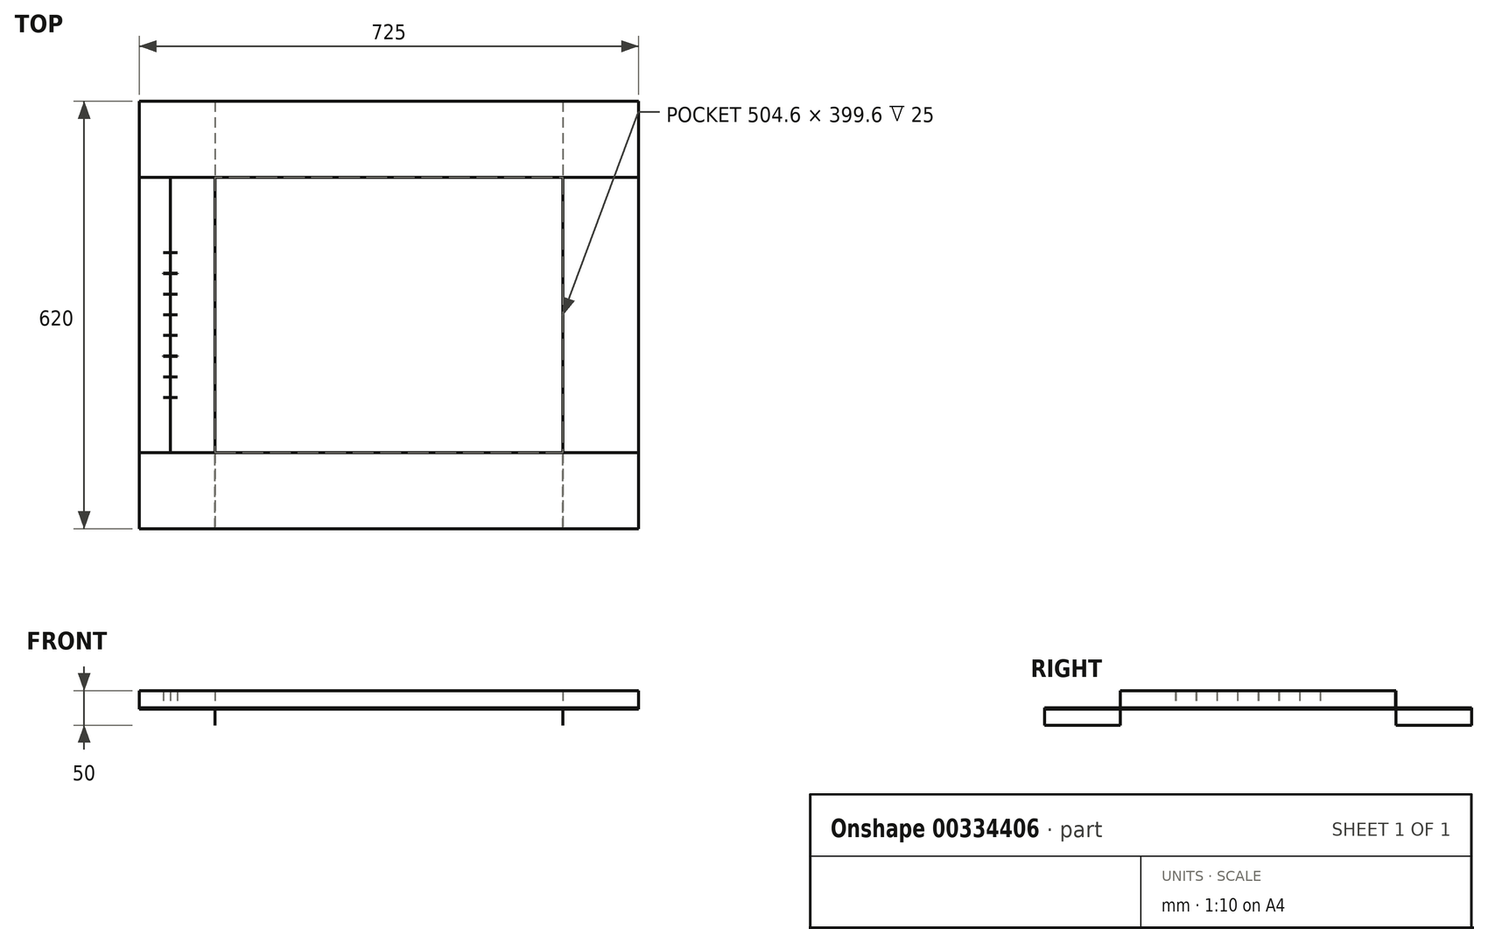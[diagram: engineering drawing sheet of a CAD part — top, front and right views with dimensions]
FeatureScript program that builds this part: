
annotation { "Feature Type Name" : "Feature", "Feature Type Description" : "" }
export const myFeature = defineFeature(function(context is Context, id is Id, definition is map)
    precondition{}
    {
        {
            var Q0;
            Q0=qCreatedBy(makeId("Top.planeOp"),FACE);
            var sketch = newSketch(context, id + "F0", { "sketchPlane" : qUnion([Q0])});
            skLineSegment(sketch, "E0.bottom", {"start": v(0, 0) * mm, "end": v(725, 0) * mm});
            skLineSegment(sketch, "E0.top", {"start": v(0, 620) * mm, "end": v(725, 620) * mm});
            skLineSegment(sketch, "E0.left", {"start": v(0, 0) * mm, "end": v(0, 620) * mm});
            skLineSegment(sketch, "E0.right", {"start": v(725, 0) * mm, "end": v(725, 620) * mm});
            skSolve(sketch);
        }
        {
            var Q0;
            Q0=makeQuery(id+"F0.imprint","IMPRINT",FACE,{"disambiguationData":[TD([[makeQuery(id+"F0.imprint","IMPRINT",EDGE,{"derivedFrom":sQuery(id+"F0.wireOp",EDGE,"E0.bottom")}),1.0]])]});
            extrude(context, id + "F1", {"entities" : qUnion([Q0]), "depth" : 2 * mm});
        }
        {
            var Q0;
            Q0=makeQuery(id+"F1.opExtrude","CAP_FACE",FACE,{"disambiguationData":[OSD([sQuery(id+"F0.wireOp",EDGE,"E0.bottom"),sQuery(id+"F0.wireOp",EDGE,"E0.top"),sQuery(id+"F0.wireOp",EDGE,"E0.left"),sQuery(id+"F0.wireOp",EDGE,"E0.right")])],"isStart":false});
            var sketch = newSketch(context, id + "F2", { "sketchPlane" : qUnion([Q0])});
            skLineSegment(sketch, "E1", {"start": v(0, 510) * mm, "end": v(725, 510) * mm});
            skLineSegment(sketch, "E2", {"start": v(0, 509.8) * mm, "end": v(725, 509.8) * mm});
            skLineSegment(sketch, "E3", {"start": v(0, 110) * mm, "end": v(725, 110) * mm});
            skLineSegment(sketch, "E4", {"start": v(0, 110.2) * mm, "end": v(725, 110.2) * mm});
            skLineSegment(sketch, "E5", {"start": v(615, 620) * mm, "end": v(615, 0) * mm});
            skLineSegment(sketch, "E6", {"start": v(110, 620) * mm, "end": v(110, 0) * mm});
            skLineSegment(sketch, "E7", {"start": v(110.2, 509.8) * mm, "end": v(110.2, 110) * mm});
            skLineSegment(sketch, "E8", {"start": v(614.8, 509.8) * mm, "end": v(614.8, 110) * mm});
            skLineSegment(sketch, "E9", {"start": v(110.25, 620) * mm, "end": v(110.25, 509.8) * mm});
            skLineSegment(sketch, "E10", {"start": v(614.75, 620) * mm, "end": v(614.75, 510) * mm});
            skLineSegment(sketch, "E11", {"start": v(110.25, 0) * mm, "end": v(110.25, 110) * mm});
            skLineSegment(sketch, "E12", {"start": v(614.75, 0) * mm, "end": v(614.75, 110) * mm});
            skLineSegment(sketch, "E13", {"start": v(45.3, 509.8) * mm, "end": v(45.3, 110) * mm});
            skLineSegment(sketch, "E14", {"start": v(45.1, 509.8) * mm, "end": v(45.1, 110) * mm});
            skLineSegment(sketch, "E15", {"start": v(35.3, 460.2) * mm, "end": v(35.3, 460.4) * mm});
            skLineSegment(sketch, "E16", {"start": v(55.3, 460.2) * mm, "end": v(55.3, 460.4) * mm});
            skLineSegment(sketch, "E17.1.0.2", {"start": v(55.3, 430.2) * mm, "end": v(55.3, 430.4) * mm});
            skLineSegment(sketch, "E17.1.0.3", {"start": v(35.3, 430.2) * mm, "end": v(35.3, 430.4) * mm});
            skLineSegment(sketch, "E17.2.0.2", {"start": v(55.3, 400.2) * mm, "end": v(55.3, 400.4) * mm});
            skLineSegment(sketch, "E17.2.0.3", {"start": v(35.3, 400.2) * mm, "end": v(35.3, 400.4) * mm});
            skLineSegment(sketch, "E17.3.0.2", {"start": v(55.3, 370.2) * mm, "end": v(55.3, 370.4) * mm});
            skLineSegment(sketch, "E17.3.0.3", {"start": v(35.3, 370.2) * mm, "end": v(35.3, 370.4) * mm});
            skLineSegment(sketch, "E17.4.0.2", {"start": v(55.3, 340.2) * mm, "end": v(55.3, 340.4) * mm});
            skLineSegment(sketch, "E17.4.0.3", {"start": v(35.3, 340.2) * mm, "end": v(35.3, 340.4) * mm});
            skLineSegment(sketch, "E17.5.0.2", {"start": v(55.3, 310.2) * mm, "end": v(55.3, 310.4) * mm});
            skLineSegment(sketch, "E17.5.0.3", {"start": v(35.3, 310.2) * mm, "end": v(35.3, 310.4) * mm});
            skLineSegment(sketch, "E17.6.0.2", {"start": v(55.3, 280.2) * mm, "end": v(55.3, 280.4) * mm});
            skLineSegment(sketch, "E17.6.0.3", {"start": v(35.3, 280.2) * mm, "end": v(35.3, 280.4) * mm});
            skLineSegment(sketch, "E17.7.0.2", {"start": v(55.3, 250.2) * mm, "end": v(55.3, 250.4) * mm});
            skLineSegment(sketch, "E17.7.0.3", {"start": v(35.3, 250.2) * mm, "end": v(35.3, 250.4) * mm});
            skLineSegment(sketch, "E17.8.0.2", {"start": v(55.3, 220.2) * mm, "end": v(55.3, 220.4) * mm});
            skLineSegment(sketch, "E17.8.0.3", {"start": v(35.3, 220.2) * mm, "end": v(35.3, 220.4) * mm});
            skLineSegment(sketch, "E17.9.0.2", {"start": v(55.3, 190.2) * mm, "end": v(55.3, 190.4) * mm});
            skLineSegment(sketch, "E17.9.0.3", {"start": v(35.3, 190.2) * mm, "end": v(35.3, 190.4) * mm});
            skLineSegment(sketch, "E17.direction1", {"start": v(35.3, 460.4) * mm, "end": v(35.3, 430.4) * mm, "construction": true});
            skLineSegment(sketch, "E18", {"start": v(45.1, 140.64) * mm, "end": v(45.3, 140.64) * mm});
            skLineSegment(sketch, "E19", {"start": v(35.3, 190.4) * mm, "end": v(55.3, 190.4) * mm});
            skLineSegment(sketch, "E20", {"start": v(35.3, 190.2) * mm, "end": v(55.3, 190.2) * mm});
            skLineSegment(sketch, "E21", {"start": v(35.3, 220.4) * mm, "end": v(55.3, 220.4) * mm});
            skLineSegment(sketch, "E22", {"start": v(55.3, 220.2) * mm, "end": v(35.3, 220.2) * mm});
            skLineSegment(sketch, "E23", {"start": v(35.3, 250.4) * mm, "end": v(55.3, 250.4) * mm});
            skLineSegment(sketch, "E24", {"start": v(55.3, 250.2) * mm, "end": v(35.3, 250.2) * mm});
            skLineSegment(sketch, "E25", {"start": v(35.3, 280.4) * mm, "end": v(55.3, 280.4) * mm});
            skLineSegment(sketch, "E26", {"start": v(55.3, 280.2) * mm, "end": v(35.3, 280.2) * mm});
            skLineSegment(sketch, "E27", {"start": v(35.3, 310.4) * mm, "end": v(55.3, 310.4) * mm});
            skLineSegment(sketch, "E28", {"start": v(35.3, 310.2) * mm, "end": v(55.3, 310.2) * mm});
            skLineSegment(sketch, "E29", {"start": v(35.3, 340.4) * mm, "end": v(55.3, 340.4) * mm});
            skLineSegment(sketch, "E30", {"start": v(55.3, 340.2) * mm, "end": v(35.3, 340.2) * mm});
            skLineSegment(sketch, "E31", {"start": v(35.3, 370.4) * mm, "end": v(55.3, 370.4) * mm});
            skLineSegment(sketch, "E32", {"start": v(55.3, 370.2) * mm, "end": v(35.3, 370.2) * mm});
            skLineSegment(sketch, "E33", {"start": v(35.3, 400.4) * mm, "end": v(55.3, 400.4) * mm});
            skLineSegment(sketch, "E34", {"start": v(55.3, 400.2) * mm, "end": v(35.3, 400.2) * mm});
            skSolve(sketch);
        }
        {
            var Q0;
            {var subQ0=sQuery(id+"F2.wireOp",EDGE,"E10");Q0=makeQuery(id+"F2.imprint","IMPRINT",FACE,{"disambiguationData":[TD([[makeQuery(id+"F2.imprint","IMPRINT",EDGE,{"derivedFrom":subQ0}),1.0]])]});}
            var Q1;
            {var subQ0=sQuery(id+"F2.wireOp",EDGE,"E6");var subQ1=sQuery(id+"F2.wireOp",EDGE,"E1");var subQ2=makeQuery(id+"F2.imprint","INTERSECT",VERTEX,{"derivedFrom":[subQ1,subQ0]});Q1=makeQuery(id+"F2.imprint","IMPRINT",FACE,{"disambiguationData":[TD([[makeQuery(id+"F2.imprint","IMPRINT",EDGE,{"disambiguationData":[TD([[subQ2,-1.0]])],"derivedFrom":subQ1}),1.0]])]});}
            var Q2;
            {var subQ0=sQuery(id+"F2.wireOp",EDGE,"E11");Q2=makeQuery(id+"F2.imprint","IMPRINT",FACE,{"disambiguationData":[TD([[makeQuery(id+"F2.imprint","IMPRINT",EDGE,{"derivedFrom":subQ0}),1.0]])]});}
            var Q3;
            {var subQ6=sQuery(id+"F2.wireOp",EDGE,"E12");Q3=makeQuery(id+"F2.imprint","IMPRINT",FACE,{"disambiguationData":[TD([[makeQuery(id+"F2.imprint","IMPRINT",EDGE,{"derivedFrom":subQ6}),-1.0]])]});}
            extrude(context, id + "F3", {"entities" : qUnion([Q0, Q1, Q2, Q3]), "operationType" : NewBodyOperationType.ADD, "oppositeDirection" : true, "depth" : 25 * mm});
        }
        {
            var Q0;
            {var subQ5=makeQuery(id+"F1.opExtrude","CAP_EDGE",EDGE,{"disambiguationData":[OSD([sQuery(id+"F0.wireOp",EDGE,"E0.left")])],"isStart":false});var subQ7=sQuery(id+"F2.wireOp",EDGE,"E1");var subQ8=makeQuery(id+"F2.imprint","INTERSECT",VERTEX,{"derivedFrom":[subQ5,subQ7]});Q0=makeQuery(id+"F2.imprint","IMPRINT",FACE,{"disambiguationData":[TD([[makeQuery(id+"F2.imprint","IMPRINT",EDGE,{"disambiguationData":[TD([[subQ8,-1.0]])],"derivedFrom":subQ7}),-1.0]])]});}
            var Q1;
            {var subQ6=sQuery(id+"F2.wireOp",EDGE,"E1");var subQ8=makeQuery(id+"F2.imprint","INTERSECT",VERTEX,{"derivedFrom":[subQ6,sQuery(id+"F2.wireOp",EDGE,"E10")]});Q1=makeQuery(id+"F2.imprint","IMPRINT",FACE,{"disambiguationData":[TD([[makeQuery(id+"F2.imprint","IMPRINT",EDGE,{"disambiguationData":[TD([[subQ8,1.0]])],"derivedFrom":subQ6}),-1.0]])]});}
            extrude(context, id + "F4", {"entities" : qUnion([Q0, Q1]), "operationType" : NewBodyOperationType.ADD, "depth" : 25 * mm});
        }
        {
            var Q0;
            {var subQ0=sQuery(id+"F2.wireOp",EDGE,"E1");var subQ1=makeQuery(id+"F1.opExtrude","CAP_EDGE",EDGE,{"disambiguationData":[OSD([sQuery(id+"F0.wireOp",EDGE,"E0.right")])],"isStart":false});var subQ2=makeQuery(id+"F2.imprint","INTERSECT",VERTEX,{"derivedFrom":[subQ1,subQ0]});Q0=makeQuery(id+"F2.imprint","IMPRINT",FACE,{"disambiguationData":[TD([[makeQuery(id+"F2.imprint","IMPRINT",EDGE,{"disambiguationData":[TD([[subQ2,1.0]])],"derivedFrom":subQ0}),-1.0]])]});}
            var Q1;
            {var subQ0=sQuery(id+"F2.wireOp",EDGE,"E8");var subQ1=sQuery(id+"F2.wireOp",EDGE,"E2");var subQ2=makeQuery(id+"F2.imprint","INTERSECT",VERTEX,{"derivedFrom":[subQ1,subQ0]});Q1=makeQuery(id+"F2.imprint","IMPRINT",FACE,{"disambiguationData":[TD([[makeQuery(id+"F2.imprint","IMPRINT",EDGE,{"disambiguationData":[TD([[subQ2,-1.0]])],"derivedFrom":subQ1}),-1.0]])]});}
            extrude(context, id + "F5", {"entities" : qUnion([Q0, Q1]), "operationType" : NewBodyOperationType.ADD, "depth" : 25 * mm});
        }
        {
            var Q0;
            {var subQ0=sQuery(id+"F2.wireOp",EDGE,"E3");var subQ1=makeQuery(id+"F1.opExtrude","CAP_EDGE",EDGE,{"disambiguationData":[OSD([sQuery(id+"F0.wireOp",EDGE,"E0.right")])],"isStart":false});var subQ2=makeQuery(id+"F2.imprint","INTERSECT",VERTEX,{"derivedFrom":[subQ1,subQ0]});Q0=makeQuery(id+"F2.imprint","IMPRINT",FACE,{"disambiguationData":[TD([[makeQuery(id+"F2.imprint","IMPRINT",EDGE,{"disambiguationData":[TD([[subQ2,1.0]])],"derivedFrom":subQ0}),1.0]])]});}
            var Q1;
            {var subQ0=sQuery(id+"F2.wireOp",EDGE,"E7");var subQ5=sQuery(id+"F2.wireOp",EDGE,"E3");var subQ9=makeQuery(id+"F2.imprint","INTERSECT",VERTEX,{"derivedFrom":[subQ5,subQ0]});Q1=makeQuery(id+"F2.imprint","IMPRINT",FACE,{"disambiguationData":[TD([[makeQuery(id+"F2.imprint","IMPRINT",EDGE,{"disambiguationData":[TD([[subQ9,-1.0]])],"derivedFrom":subQ5}),1.0]])]});}
            var Q2;
            {var subQ0=sQuery(id+"F2.wireOp",EDGE,"E8");var subQ1=sQuery(id+"F2.wireOp",EDGE,"E3");var subQ2=makeQuery(id+"F2.imprint","INTERSECT",VERTEX,{"derivedFrom":[subQ1,subQ0]});Q2=makeQuery(id+"F2.imprint","IMPRINT",FACE,{"disambiguationData":[TD([[makeQuery(id+"F2.imprint","IMPRINT",EDGE,{"disambiguationData":[TD([[subQ2,-1.0]])],"derivedFrom":subQ1}),1.0]])]});}
            var Q3;
            {var subQ0=sQuery(id+"F2.wireOp",EDGE,"E13");var subQ1=sQuery(id+"F2.wireOp",EDGE,"E3");var subQ2=makeQuery(id+"F2.imprint","INTERSECT",VERTEX,{"derivedFrom":[subQ1,subQ0]});Q3=makeQuery(id+"F2.imprint","IMPRINT",FACE,{"disambiguationData":[TD([[makeQuery(id+"F2.imprint","IMPRINT",EDGE,{"disambiguationData":[TD([[subQ2,-1.0]])],"derivedFrom":subQ1}),1.0]])]});}
            var Q4;
            {var subQ0=sQuery(id+"F2.wireOp",EDGE,"E7");var subQ1=sQuery(id+"F2.wireOp",EDGE,"E3");var subQ2=makeQuery(id+"F2.imprint","INTERSECT",VERTEX,{"derivedFrom":[subQ1,subQ0]});Q4=makeQuery(id+"F2.imprint","IMPRINT",FACE,{"disambiguationData":[TD([[makeQuery(id+"F2.imprint","IMPRINT",EDGE,{"disambiguationData":[TD([[subQ2,1.0]])],"derivedFrom":subQ1}),1.0]])]});}
            extrude(context, id + "F6", {"entities" : qUnion([Q0, Q1, Q2, Q3, Q4]), "operationType" : NewBodyOperationType.ADD, "depth" : 25 * mm});
        }
        {
            var Q0;
            {var subQ0=sQuery(id+"F2.wireOp",EDGE,"E3");var subQ1=makeQuery(id+"F1.opExtrude","CAP_EDGE",EDGE,{"disambiguationData":[OSD([sQuery(id+"F0.wireOp",EDGE,"E0.left")])],"isStart":false});var subQ2=makeQuery(id+"F2.imprint","INTERSECT",VERTEX,{"derivedFrom":[subQ1,subQ0]});Q0=makeQuery(id+"F2.imprint","IMPRINT",FACE,{"disambiguationData":[TD([[makeQuery(id+"F2.imprint","IMPRINT",EDGE,{"disambiguationData":[TD([[subQ2,-1.0]])],"derivedFrom":subQ0}),1.0]])]});}
            extrude(context, id + "F7", {"entities" : qUnion([Q0]), "operationType" : NewBodyOperationType.ADD, "depth" : 25 * mm});
        }
        {
            var Q0;
            {var subQ0=sQuery(id+"F2.wireOp",EDGE,"E18");Q0=makeQuery(id+"F2.imprint","IMPRINT",FACE,{"disambiguationData":[TD([[makeQuery(id+"F2.imprint","IMPRINT",EDGE,{"derivedFrom":subQ0}),1.0]])]});}
            extrude(context, id + "F8", {"entities" : qUnion([Q0]), "operationType" : NewBodyOperationType.ADD, "depth" : 25 * mm});
        }
        {
            var Q0;
            {var subQ0=sQuery(id+"F2.wireOp",EDGE,"E18");Q0=makeQuery(id+"F2.imprint","IMPRINT",FACE,{"disambiguationData":[TD([[makeQuery(id+"F2.imprint","IMPRINT",EDGE,{"derivedFrom":subQ0}),1.0]])]});}
            var Q1;
            {var subQ5=sQuery(id+"F2.wireOp",EDGE,"E17.9.0.3");Q1=makeQuery(id+"F2.imprint","IMPRINT",FACE,{"disambiguationData":[TD([[makeQuery(id+"F2.imprint","IMPRINT",EDGE,{"derivedFrom":subQ5}),-1.0]])]});}
            var Q2;
            {var subQ5=sQuery(id+"F2.wireOp",EDGE,"E17.9.0.2");Q2=makeQuery(id+"F2.imprint","IMPRINT",FACE,{"disambiguationData":[TD([[makeQuery(id+"F2.imprint","IMPRINT",EDGE,{"derivedFrom":subQ5}),1.0]])]});}
            var Q3;
            {var subQ0=sQuery(id+"F2.wireOp",EDGE,"E17.8.0.0");var subQ1=sQuery(id+"F2.wireOp",EDGE,"E13");var subQ2=makeQuery(id+"F2.imprint","INTERSECT",VERTEX,{"derivedFrom":[subQ1,subQ0]});Q3=makeQuery(id+"F2.imprint","IMPRINT",FACE,{"disambiguationData":[TD([[makeQuery(id+"F2.imprint","IMPRINT",EDGE,{"disambiguationData":[TD([[subQ2,-1.0]])],"derivedFrom":subQ1}),-1.0]])]});}
            var Q4;
            {var subQ0=sQuery(id+"F2.wireOp",EDGE,"E17.9.0.1");var subQ1=sQuery(id+"F2.wireOp",EDGE,"E13");var subQ2=makeQuery(id+"F2.imprint","INTERSECT",VERTEX,{"derivedFrom":[subQ1,subQ0]});Q4=makeQuery(id+"F2.imprint","IMPRINT",FACE,{"disambiguationData":[TD([[makeQuery(id+"F2.imprint","IMPRINT",EDGE,{"disambiguationData":[TD([[subQ2,-1.0]])],"derivedFrom":subQ1}),-1.0]])]});}
            var Q5;
            {var subQ5=sQuery(id+"F2.wireOp",EDGE,"E17.8.0.3");Q5=makeQuery(id+"F2.imprint","IMPRINT",FACE,{"disambiguationData":[TD([[makeQuery(id+"F2.imprint","IMPRINT",EDGE,{"derivedFrom":subQ5}),-1.0]])]});}
            var Q6;
            {var subQ5=sQuery(id+"F2.wireOp",EDGE,"E17.8.0.2");Q6=makeQuery(id+"F2.imprint","IMPRINT",FACE,{"disambiguationData":[TD([[makeQuery(id+"F2.imprint","IMPRINT",EDGE,{"derivedFrom":subQ5}),1.0]])]});}
            var Q7;
            {var subQ0=sQuery(id+"F2.wireOp",EDGE,"E17.8.0.1");var subQ1=sQuery(id+"F2.wireOp",EDGE,"E13");var subQ2=makeQuery(id+"F2.imprint","INTERSECT",VERTEX,{"derivedFrom":[subQ1,subQ0]});Q7=makeQuery(id+"F2.imprint","IMPRINT",FACE,{"disambiguationData":[TD([[makeQuery(id+"F2.imprint","IMPRINT",EDGE,{"disambiguationData":[TD([[subQ2,-1.0]])],"derivedFrom":subQ1}),-1.0]])]});}
            var Q8;
            {var subQ0=sQuery(id+"F2.wireOp",EDGE,"E17.7.0.0");var subQ1=sQuery(id+"F2.wireOp",EDGE,"E13");var subQ2=makeQuery(id+"F2.imprint","INTERSECT",VERTEX,{"derivedFrom":[subQ1,subQ0]});Q8=makeQuery(id+"F2.imprint","IMPRINT",FACE,{"disambiguationData":[TD([[makeQuery(id+"F2.imprint","IMPRINT",EDGE,{"disambiguationData":[TD([[subQ2,-1.0]])],"derivedFrom":subQ1}),-1.0]])]});}
            var Q9;
            {var subQ5=sQuery(id+"F2.wireOp",EDGE,"E17.7.0.3");Q9=makeQuery(id+"F2.imprint","IMPRINT",FACE,{"disambiguationData":[TD([[makeQuery(id+"F2.imprint","IMPRINT",EDGE,{"derivedFrom":subQ5}),-1.0]])]});}
            var Q10;
            {var subQ5=sQuery(id+"F2.wireOp",EDGE,"E17.7.0.2");Q10=makeQuery(id+"F2.imprint","IMPRINT",FACE,{"disambiguationData":[TD([[makeQuery(id+"F2.imprint","IMPRINT",EDGE,{"derivedFrom":subQ5}),1.0]])]});}
            var Q11;
            {var subQ0=sQuery(id+"F2.wireOp",EDGE,"E17.7.0.1");var subQ1=sQuery(id+"F2.wireOp",EDGE,"E13");var subQ2=makeQuery(id+"F2.imprint","INTERSECT",VERTEX,{"derivedFrom":[subQ1,subQ0]});Q11=makeQuery(id+"F2.imprint","IMPRINT",FACE,{"disambiguationData":[TD([[makeQuery(id+"F2.imprint","IMPRINT",EDGE,{"disambiguationData":[TD([[subQ2,-1.0]])],"derivedFrom":subQ1}),-1.0]])]});}
            var Q12;
            {var subQ0=sQuery(id+"F2.wireOp",EDGE,"E17.6.0.0");var subQ1=sQuery(id+"F2.wireOp",EDGE,"E13");var subQ2=makeQuery(id+"F2.imprint","INTERSECT",VERTEX,{"derivedFrom":[subQ1,subQ0]});Q12=makeQuery(id+"F2.imprint","IMPRINT",FACE,{"disambiguationData":[TD([[makeQuery(id+"F2.imprint","IMPRINT",EDGE,{"disambiguationData":[TD([[subQ2,-1.0]])],"derivedFrom":subQ1}),-1.0]])]});}
            var Q13;
            {var subQ5=sQuery(id+"F2.wireOp",EDGE,"E17.6.0.3");Q13=makeQuery(id+"F2.imprint","IMPRINT",FACE,{"disambiguationData":[TD([[makeQuery(id+"F2.imprint","IMPRINT",EDGE,{"derivedFrom":subQ5}),-1.0]])]});}
            var Q14;
            {var subQ5=sQuery(id+"F2.wireOp",EDGE,"E17.6.0.2");Q14=makeQuery(id+"F2.imprint","IMPRINT",FACE,{"disambiguationData":[TD([[makeQuery(id+"F2.imprint","IMPRINT",EDGE,{"derivedFrom":subQ5}),1.0]])]});}
            var Q15;
            {var subQ0=sQuery(id+"F2.wireOp",EDGE,"E17.6.0.1");var subQ1=sQuery(id+"F2.wireOp",EDGE,"E13");var subQ2=makeQuery(id+"F2.imprint","INTERSECT",VERTEX,{"derivedFrom":[subQ1,subQ0]});Q15=makeQuery(id+"F2.imprint","IMPRINT",FACE,{"disambiguationData":[TD([[makeQuery(id+"F2.imprint","IMPRINT",EDGE,{"disambiguationData":[TD([[subQ2,-1.0]])],"derivedFrom":subQ1}),-1.0]])]});}
            var Q16;
            {var subQ0=sQuery(id+"F2.wireOp",EDGE,"E17.5.0.0");var subQ1=sQuery(id+"F2.wireOp",EDGE,"E13");var subQ2=makeQuery(id+"F2.imprint","INTERSECT",VERTEX,{"derivedFrom":[subQ1,subQ0]});Q16=makeQuery(id+"F2.imprint","IMPRINT",FACE,{"disambiguationData":[TD([[makeQuery(id+"F2.imprint","IMPRINT",EDGE,{"disambiguationData":[TD([[subQ2,-1.0]])],"derivedFrom":subQ1}),-1.0]])]});}
            var Q17;
            {var subQ5=sQuery(id+"F2.wireOp",EDGE,"E17.5.0.3");Q17=makeQuery(id+"F2.imprint","IMPRINT",FACE,{"disambiguationData":[TD([[makeQuery(id+"F2.imprint","IMPRINT",EDGE,{"derivedFrom":subQ5}),-1.0]])]});}
            var Q18;
            {var subQ0=sQuery(id+"F2.wireOp",EDGE,"E17.5.0.1");var subQ1=sQuery(id+"F2.wireOp",EDGE,"E13");var subQ2=makeQuery(id+"F2.imprint","INTERSECT",VERTEX,{"derivedFrom":[subQ1,subQ0]});Q18=makeQuery(id+"F2.imprint","IMPRINT",FACE,{"disambiguationData":[TD([[makeQuery(id+"F2.imprint","IMPRINT",EDGE,{"disambiguationData":[TD([[subQ2,-1.0]])],"derivedFrom":subQ1}),-1.0]])]});}
            var Q19;
            {var subQ5=sQuery(id+"F2.wireOp",EDGE,"E17.5.0.2");Q19=makeQuery(id+"F2.imprint","IMPRINT",FACE,{"disambiguationData":[TD([[makeQuery(id+"F2.imprint","IMPRINT",EDGE,{"derivedFrom":subQ5}),1.0]])]});}
            var Q20;
            {var subQ0=sQuery(id+"F2.wireOp",EDGE,"E17.4.0.0");var subQ1=sQuery(id+"F2.wireOp",EDGE,"E13");var subQ2=makeQuery(id+"F2.imprint","INTERSECT",VERTEX,{"derivedFrom":[subQ1,subQ0]});Q20=makeQuery(id+"F2.imprint","IMPRINT",FACE,{"disambiguationData":[TD([[makeQuery(id+"F2.imprint","IMPRINT",EDGE,{"disambiguationData":[TD([[subQ2,-1.0]])],"derivedFrom":subQ1}),-1.0]])]});}
            var Q21;
            {var subQ5=sQuery(id+"F2.wireOp",EDGE,"E17.4.0.3");Q21=makeQuery(id+"F2.imprint","IMPRINT",FACE,{"disambiguationData":[TD([[makeQuery(id+"F2.imprint","IMPRINT",EDGE,{"derivedFrom":subQ5}),-1.0]])]});}
            var Q22;
            {var subQ0=sQuery(id+"F2.wireOp",EDGE,"E17.4.0.1");var subQ1=sQuery(id+"F2.wireOp",EDGE,"E13");var subQ2=makeQuery(id+"F2.imprint","INTERSECT",VERTEX,{"derivedFrom":[subQ1,subQ0]});Q22=makeQuery(id+"F2.imprint","IMPRINT",FACE,{"disambiguationData":[TD([[makeQuery(id+"F2.imprint","IMPRINT",EDGE,{"disambiguationData":[TD([[subQ2,-1.0]])],"derivedFrom":subQ1}),-1.0]])]});}
            var Q23;
            {var subQ5=sQuery(id+"F2.wireOp",EDGE,"E17.4.0.2");Q23=makeQuery(id+"F2.imprint","IMPRINT",FACE,{"disambiguationData":[TD([[makeQuery(id+"F2.imprint","IMPRINT",EDGE,{"derivedFrom":subQ5}),1.0]])]});}
            var Q24;
            {var subQ0=sQuery(id+"F2.wireOp",EDGE,"E17.3.0.0");var subQ1=sQuery(id+"F2.wireOp",EDGE,"E13");var subQ2=makeQuery(id+"F2.imprint","INTERSECT",VERTEX,{"derivedFrom":[subQ1,subQ0]});Q24=makeQuery(id+"F2.imprint","IMPRINT",FACE,{"disambiguationData":[TD([[makeQuery(id+"F2.imprint","IMPRINT",EDGE,{"disambiguationData":[TD([[subQ2,-1.0]])],"derivedFrom":subQ1}),-1.0]])]});}
            var Q25;
            {var subQ5=sQuery(id+"F2.wireOp",EDGE,"E17.3.0.3");Q25=makeQuery(id+"F2.imprint","IMPRINT",FACE,{"disambiguationData":[TD([[makeQuery(id+"F2.imprint","IMPRINT",EDGE,{"derivedFrom":subQ5}),-1.0]])]});}
            var Q26;
            {var subQ0=sQuery(id+"F2.wireOp",EDGE,"E17.3.0.1");var subQ1=sQuery(id+"F2.wireOp",EDGE,"E13");var subQ2=makeQuery(id+"F2.imprint","INTERSECT",VERTEX,{"derivedFrom":[subQ1,subQ0]});Q26=makeQuery(id+"F2.imprint","IMPRINT",FACE,{"disambiguationData":[TD([[makeQuery(id+"F2.imprint","IMPRINT",EDGE,{"disambiguationData":[TD([[subQ2,-1.0]])],"derivedFrom":subQ1}),-1.0]])]});}
            var Q27;
            {var subQ5=sQuery(id+"F2.wireOp",EDGE,"E17.3.0.2");Q27=makeQuery(id+"F2.imprint","IMPRINT",FACE,{"disambiguationData":[TD([[makeQuery(id+"F2.imprint","IMPRINT",EDGE,{"derivedFrom":subQ5}),1.0]])]});}
            var Q28;
            {var subQ0=sQuery(id+"F2.wireOp",EDGE,"E17.2.0.0");var subQ1=sQuery(id+"F2.wireOp",EDGE,"E13");var subQ2=makeQuery(id+"F2.imprint","INTERSECT",VERTEX,{"derivedFrom":[subQ1,subQ0]});Q28=makeQuery(id+"F2.imprint","IMPRINT",FACE,{"disambiguationData":[TD([[makeQuery(id+"F2.imprint","IMPRINT",EDGE,{"disambiguationData":[TD([[subQ2,-1.0]])],"derivedFrom":subQ1}),-1.0]])]});}
            var Q29;
            {var subQ5=sQuery(id+"F2.wireOp",EDGE,"E17.2.0.3");Q29=makeQuery(id+"F2.imprint","IMPRINT",FACE,{"disambiguationData":[TD([[makeQuery(id+"F2.imprint","IMPRINT",EDGE,{"derivedFrom":subQ5}),-1.0]])]});}
            var Q30;
            {var subQ0=sQuery(id+"F2.wireOp",EDGE,"E17.2.0.1");var subQ1=sQuery(id+"F2.wireOp",EDGE,"E13");var subQ2=makeQuery(id+"F2.imprint","INTERSECT",VERTEX,{"derivedFrom":[subQ1,subQ0]});Q30=makeQuery(id+"F2.imprint","IMPRINT",FACE,{"disambiguationData":[TD([[makeQuery(id+"F2.imprint","IMPRINT",EDGE,{"disambiguationData":[TD([[subQ2,-1.0]])],"derivedFrom":subQ1}),-1.0]])]});}
            var Q31;
            {var subQ5=sQuery(id+"F2.wireOp",EDGE,"E17.2.0.2");Q31=makeQuery(id+"F2.imprint","IMPRINT",FACE,{"disambiguationData":[TD([[makeQuery(id+"F2.imprint","IMPRINT",EDGE,{"derivedFrom":subQ5}),1.0]])]});}
            var Q32;
            {var subQ0=sQuery(id+"F2.wireOp",EDGE,"E17.1.0.0");var subQ1=sQuery(id+"F2.wireOp",EDGE,"E13");var subQ2=makeQuery(id+"F2.imprint","INTERSECT",VERTEX,{"derivedFrom":[subQ1,subQ0]});Q32=makeQuery(id+"F2.imprint","IMPRINT",FACE,{"disambiguationData":[TD([[makeQuery(id+"F2.imprint","IMPRINT",EDGE,{"disambiguationData":[TD([[subQ2,-1.0]])],"derivedFrom":subQ1}),-1.0]])]});}
            var Q33;
            {var subQ5=sQuery(id+"F2.wireOp",EDGE,"E17.1.0.3");Q33=makeQuery(id+"F2.imprint","IMPRINT",FACE,{"disambiguationData":[TD([[makeQuery(id+"F2.imprint","IMPRINT",EDGE,{"derivedFrom":subQ5}),-1.0]])]});}
            var Q34;
            {var subQ0=sQuery(id+"F2.wireOp",EDGE,"E17.1.0.1");var subQ1=sQuery(id+"F2.wireOp",EDGE,"E13");var subQ2=makeQuery(id+"F2.imprint","INTERSECT",VERTEX,{"derivedFrom":[subQ1,subQ0]});Q34=makeQuery(id+"F2.imprint","IMPRINT",FACE,{"disambiguationData":[TD([[makeQuery(id+"F2.imprint","IMPRINT",EDGE,{"disambiguationData":[TD([[subQ2,-1.0]])],"derivedFrom":subQ1}),-1.0]])]});}
            var Q35;
            {var subQ5=sQuery(id+"F2.wireOp",EDGE,"E17.1.0.2");Q35=makeQuery(id+"F2.imprint","IMPRINT",FACE,{"disambiguationData":[TD([[makeQuery(id+"F2.imprint","IMPRINT",EDGE,{"derivedFrom":subQ5}),1.0]])]});}
            var Q36;
            {var subQ0=sQuery(id+"F2.wireOp",EDGE,"PF9Whc2X-JOV0-p4xt-AjMA-3nAZ7eqoeYj6");var subQ1=sQuery(id+"F2.wireOp",EDGE,"E13");var subQ2=makeQuery(id+"F2.imprint","INTERSECT",VERTEX,{"derivedFrom":[subQ1,subQ0]});Q36=makeQuery(id+"F2.imprint","IMPRINT",FACE,{"disambiguationData":[TD([[makeQuery(id+"F2.imprint","IMPRINT",EDGE,{"disambiguationData":[TD([[subQ2,-1.0]])],"derivedFrom":subQ1}),-1.0]])]});}
            var Q37;
            {var subQ5=sQuery(id+"F2.wireOp",EDGE,"E15");Q37=makeQuery(id+"F2.imprint","IMPRINT",FACE,{"disambiguationData":[TD([[makeQuery(id+"F2.imprint","IMPRINT",EDGE,{"derivedFrom":subQ5}),-1.0]])]});}
            var Q38;
            {var subQ0=sQuery(id+"F2.wireOp",EDGE,"TrYL828V-23KU-50iI-e81v-BixSrFEmtcK7");var subQ1=sQuery(id+"F2.wireOp",EDGE,"E13");var subQ2=makeQuery(id+"F2.imprint","INTERSECT",VERTEX,{"derivedFrom":[subQ1,subQ0]});Q38=makeQuery(id+"F2.imprint","IMPRINT",FACE,{"disambiguationData":[TD([[makeQuery(id+"F2.imprint","IMPRINT",EDGE,{"disambiguationData":[TD([[subQ2,-1.0]])],"derivedFrom":subQ1}),-1.0]])]});}
            var Q39;
            {var subQ5=sQuery(id+"F2.wireOp",EDGE,"E16");Q39=makeQuery(id+"F2.imprint","IMPRINT",FACE,{"disambiguationData":[TD([[makeQuery(id+"F2.imprint","IMPRINT",EDGE,{"derivedFrom":subQ5}),1.0]])]});}
            var Q40;
            {var subQ0=sQuery(id+"F2.wireOp",EDGE,"E13");var subQ1=sQuery(id+"F2.wireOp",EDGE,"E2");var subQ2=makeQuery(id+"F2.imprint","INTERSECT",VERTEX,{"derivedFrom":[subQ1,subQ0]});Q40=makeQuery(id+"F2.imprint","IMPRINT",FACE,{"disambiguationData":[TD([[makeQuery(id+"F2.imprint","IMPRINT",EDGE,{"disambiguationData":[TD([[subQ2,1.0]])],"derivedFrom":subQ1}),-1.0]])]});}
            var Q41;
            {var subQ0=sQuery(id+"F2.wireOp",EDGE,"E7");var subQ1=sQuery(id+"F2.wireOp",EDGE,"E2");var subQ2=makeQuery(id+"F2.imprint","INTERSECT",VERTEX,{"derivedFrom":[subQ1,subQ0]});Q41=makeQuery(id+"F2.imprint","IMPRINT",FACE,{"disambiguationData":[TD([[makeQuery(id+"F2.imprint","IMPRINT",EDGE,{"disambiguationData":[TD([[subQ2,1.0]])],"derivedFrom":subQ1}),-1.0]])]});}
            var Q42;
            {var subQ0=sQuery(id+"F2.wireOp",EDGE,"E6");var subQ1=sQuery(id+"F2.wireOp",EDGE,"E1");var subQ2=makeQuery(id+"F2.imprint","INTERSECT",VERTEX,{"derivedFrom":[subQ1,subQ0]});Q42=makeQuery(id+"F2.imprint","IMPRINT",FACE,{"disambiguationData":[TD([[makeQuery(id+"F2.imprint","IMPRINT",EDGE,{"disambiguationData":[TD([[subQ2,-1.0]])],"derivedFrom":subQ1}),-1.0]])]});}
            var Q43;
            {var subQ5=sQuery(id+"F2.wireOp",EDGE,"E18");Q43=makeQuery(id+"F2.imprint","IMPRINT",FACE,{"disambiguationData":[TD([[makeQuery(id+"F2.imprint","IMPRINT",EDGE,{"derivedFrom":subQ5}),-1.0]])]});}
            var Q44;
            {var subQ0=sQuery(id+"F2.wireOp",EDGE,"E13");var subQ1=sQuery(id+"F2.wireOp",EDGE,"E3");var subQ2=makeQuery(id+"F2.imprint","INTERSECT",VERTEX,{"derivedFrom":[subQ1,subQ0]});Q44=makeQuery(id+"F2.imprint","IMPRINT",FACE,{"disambiguationData":[TD([[makeQuery(id+"F2.imprint","IMPRINT",EDGE,{"disambiguationData":[TD([[subQ2,1.0]])],"derivedFrom":subQ1}),1.0]])]});}
            extrude(context, id + "F9", {"entities" : qUnion([Q0, Q1, Q2, Q3, Q4, Q5, Q6, Q7, Q8, Q9, Q10, Q11, Q12, Q13, Q14, Q15, Q16, Q17, Q18, Q19, Q20, Q21, Q22, Q23, Q24, Q25, Q26, Q27, Q28, Q29, Q30, Q31, Q32, Q33, Q34, Q35, Q36, Q37, Q38, Q39, Q40, Q41, Q42, Q43, Q44]), "operationType" : NewBodyOperationType.ADD, "depth" : 25 * mm});
        }
    });
